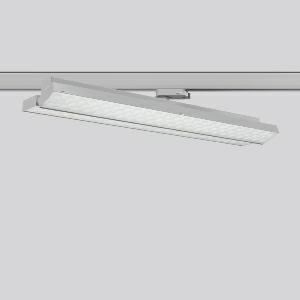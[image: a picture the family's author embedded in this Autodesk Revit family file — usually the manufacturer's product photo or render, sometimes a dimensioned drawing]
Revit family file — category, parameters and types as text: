
# Revit family: tx-move_742162_004_2_5f72
name_source: partatom
category: Lighting Fixtures
units: mm (PartAtom-declared; Revit-internal decimal feet)

## family parameters
Cut with Voids When Loaded = No
Host = Face
Light Source = No
Part Type = Normal
Room Calculation Point = No
Round Connector Dimension = Use Diameter
Shared = No

## types (1)
- MultiLumen 1 (1 x LED Modul 927, 2150 lm, 2700)
    Apparent Load = 38 VA
    CIE Flux Codes = 77 96 99 100 100
    Color Rendering = 92
    Color Temperature = 2700
    Default Elevation = 1800 mm
    Description = Series: TX-MOVE
Multifunctional surface-mounted spotlight for area lighting. Very flat design. Housing: sheet steel, powder-coated. Rotation range: 356°. Swivel range: 90°. Consistent alignment possible with visible tilt scale. High-efficiency LED units with optimum light control thanks to clear plastic (PC) lens optics. Spezielle Mikrostrukturen reduzieren Gelbsaum. Symmetrical light distribution. Best colour rendering with CRI >90 for fresh products and coloured textiles. With multi adaptor for 3-circuit tracks 230 V. Suitable for Track on ceiling. MultiLumen: Luminous flux adjustable in 3 steps. Factory setting is the highest luminous flux. Environmentally friendly and resource-saving due to replaceable and recyclable components. 
Colour: silver, matt (approx. RAL 9006)
Length: 570 mm
Width: 119 mm
Height: 92 mm
Lamp: LED
Socket: without socket
Colour temperature: 2700K
Colour rendering index (CRI): 90
System power: 38 W
Rated luminous flux: 4300 lm
Luminous efficiency: 113 lm/W
System power 2: 51 W
Rated luminous flux 2: 5600 lm
Luminous efficiency 2: 110 lm/W
System power 3: 62 W
Rated luminous flux 3: 6650 lm
Luminous efficiency 3: 107 lm/W
Control gear: Regulated power supply
Protection class: I
Type of protection: IP 20
    Height = 75 mm
    Lamp = 1 x LED Modul 927
    Lamp Light Flux = 2150 lm
    Lamp count = 1
    Length = 569 mm
    Lifetime = 50000 h
    Luminous efficacy = 113 lm/W
    Manufacturer = RZB
    ModVariant = No
    Model = 742162.004.2
    Mounting Place = Ceiling
    Mounting Type = Surface mounted
    Number of Poles = 1
    OnlyDefault = Yes
    Power Factor = 1
    Product Name = TX-MOVE
    Product group = Track mounted projectors
    ProductGroupID = 301
    Protection Class = Protection class I
    Protection Degree = IP 20
    RLX_Detail_Level = 1
    RLX_Emergency_Light_Flux = 0 lm
    RLX_Emergency_Type = 0
    RLX_Emergency_Type_DB = No
    RlxData = <blob elided: 33249 chars, md5=2a82c981>
    Socket = socket
    Standby Power = 0 W
    System Light Flux = 4300 lm
    System Power = 38 W
    Type Comments = MultiLumen 1
    Type Image = 742162.004.jpg
    URL = http://relux.com
    VarID = multilumen_1
    Voltage = 0 V
    Weight = 0.00 kg
    Width = 119 mm

## geometry (parser evidence)
native form markers: Blend x4, Sweep x15
no freeform markers — native parametric forms only
